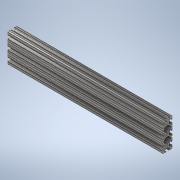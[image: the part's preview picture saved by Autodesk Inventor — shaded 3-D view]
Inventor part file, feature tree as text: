
AUTODESK INVENTOR PART (.ipt)
format: ipt  version: 2020 (Build 240168000, 168)  size: 380,928 bytes
history: native  units: in
note: dims shown in document units (in); Inventor stores cm internally (conversion verified against a paired STEP export)
features: sketch x2, extrude x1
ambient origin geometry x8: Origin, YZ Plane, XZ Plane, XY Plane, X Axis, Y Axis, Z Axis, Center Point
bodies: Solid1 (feature_tree)
feature tree (3):
  extrude  "Extrusion1"  [1 undecoded]
  sketch  "Sketch2"
  sketch  "Sketch1"  dims[d0=16.0in d1=0.0in]
note: 1 required parameter value undecoded (feature->parameter linkage not recoverable at this tier; creation-order binding heuristic only, values carry confidence <= 0.55)
